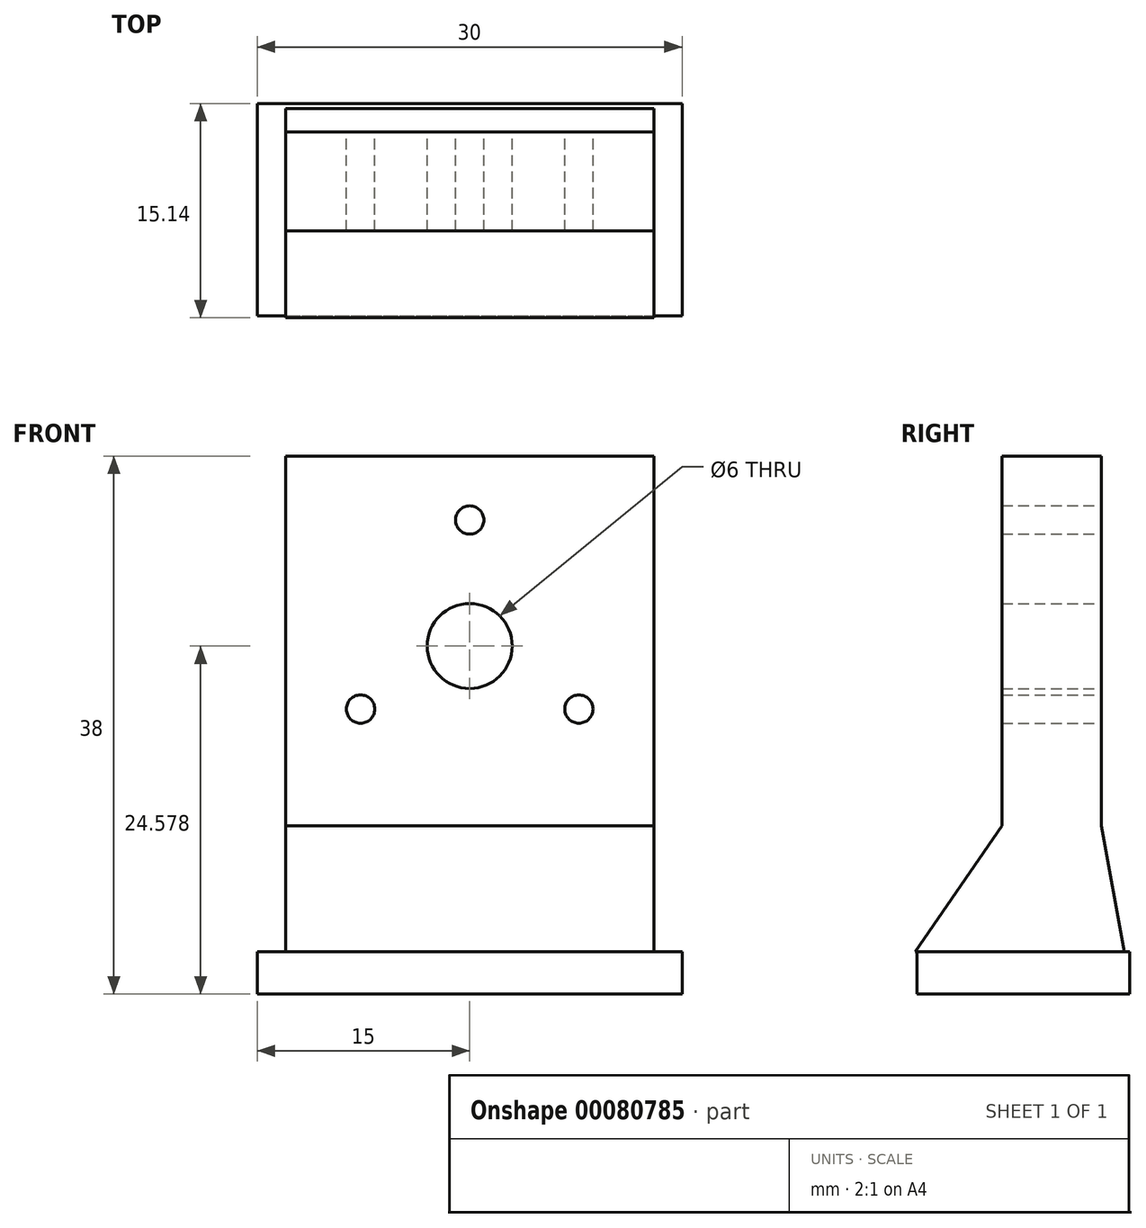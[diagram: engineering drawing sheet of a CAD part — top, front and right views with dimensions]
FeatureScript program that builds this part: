
annotation { "Feature Type Name" : "Feature", "Feature Type Description" : "" }
export const myFeature = defineFeature(function(context is Context, id is Id, definition is map)
    precondition{}
    {
        {
            var Q0;
            Q0=qCreatedBy(makeId("Front.planeOp"),FACE);
            var sketch = newSketch(context, id + "F0", { "sketchPlane" : qUnion([Q0])});
            skLineSegment(sketch, "E0.bottom", {"start": v(-13, 0) * mm, "end": v(13, 0) * mm});
            skLineSegment(sketch, "E0.top", {"start": v(-13, 35) * mm, "end": v(13, 35) * mm});
            skLineSegment(sketch, "E0.left", {"start": v(-13, 0) * mm, "end": v(-13, 35) * mm});
            skLineSegment(sketch, "E0.right", {"start": v(13, 0) * mm, "end": v(13, 35) * mm});
            skPoint(sketch, "E1", {"position": v(0, 0) * mm});
            skCircle(sketch, "E2", {"center": v(0, 21.58) * mm, "radius": 3 * mm});
            skCircle(sketch, "E3", {"center": v(0, 21.58) * mm, "radius": 8.9 * mm, "construction": true});
            skCircle(sketch, "E4", {"center": v(0, 30.48) * mm, "radius": 1 * mm});
            skCircle(sketch, "E5.1.0", {"center": v(-7.7, 17.13) * mm, "radius": 1 * mm});
            skCircle(sketch, "E5.2.0", {"center": v(7.7, 17.13) * mm, "radius": 1 * mm});
            skSolve(sketch);
        }
        {
            var Q0;
            Q0=makeQuery(id+"F0.imprint","IMPRINT",FACE,{"disambiguationData":[TD([[makeQuery(id+"F0.imprint","IMPRINT",EDGE,{"derivedFrom":sQuery(id+"F0.wireOp",EDGE,"E0.bottom")}),1.0]])]});
            extrude(context, id + "F1", {"entities" : qUnion([Q0]), "depth" : 7 * mm});
        }
        {
            var Q0;
            Q0=qCreatedBy(makeId("Top.planeOp"),FACE);
            var sketch = newSketch(context, id + "F2", { "sketchPlane" : qUnion([Q0])});
            skLineSegment(sketch, "E6.bottom", {"start": v(-15, 2) * mm, "end": v(15, 2) * mm});
            skLineSegment(sketch, "E6.top", {"start": v(-15, -13) * mm, "end": v(15, -13) * mm});
            skLineSegment(sketch, "E6.left", {"start": v(-15, 2) * mm, "end": v(-15, -13) * mm});
            skLineSegment(sketch, "E6.right", {"start": v(15, 2) * mm, "end": v(15, -13) * mm});
            skSolve(sketch);
        }
        {
            var Q0;
            Q0=makeQuery(id+"F2.imprint","IMPRINT",FACE,{"disambiguationData":[TD([[makeQuery(id+"F2.imprint","IMPRINT",EDGE,{"derivedFrom":sQuery(id+"F2.wireOp",EDGE,"E6.bottom")}),-1.0]])]});
            extrude(context, id + "F3", {"entities" : qUnion([Q0]), "operationType" : NewBodyOperationType.ADD, "oppositeDirection" : true, "depth" : 3 * mm});
        }
        {
            var Q0;
            Q0=makeQuery(id+"F1.opExtrude","SWEPT_FACE",FACE,{"disambiguationData":[OSD([sQuery(id+"F0.wireOp",EDGE,"E0.left")])]});
            var sketch = newSketch(context, id + "F4", { "sketchPlane" : qUnion([Q0])});
            skLineSegment(sketch, "E7", {"start": v(7, 8.88) * mm, "end": v(13.14, 0) * mm});
            skLineSegment(sketch, "E8", {"start": v(7, 6.87) * mm, "end": v(11.75, 0) * mm});
            skLineSegment(sketch, "E9", {"start": v(7, 4.17) * mm, "end": v(9.88, 0) * mm});
            skLineSegment(sketch, "E10", {"start": v(7, 1.96) * mm, "end": v(8.36, 0) * mm});
            skLineSegment(sketch, "E11", {"start": v(7, 4.17) * mm, "end": v(7, 1.96) * mm});
            skLineSegment(sketch, "E12", {"start": v(7, 8.88) * mm, "end": v(7, 6.87) * mm});
            skLineSegment(sketch, "E13", {"start": v(13.14, 0) * mm, "end": v(11.75, 0) * mm});
            skLineSegment(sketch, "E14", {"start": v(9.88, 0) * mm, "end": v(8.36, 0) * mm});
            skLineSegment(sketch, "E15", {"start": v(0, 8.88) * mm, "end": v(-1.63, 0) * mm});
            skLineSegment(sketch, "E16", {"start": v(0, 4.23) * mm, "end": v(-0.78, 0) * mm});
            skLineSegment(sketch, "E17", {"start": v(0, 8.88) * mm, "end": v(0, 4.23) * mm});
            skLineSegment(sketch, "E18", {"start": v(-1.63, 0) * mm, "end": v(-0.78, 0) * mm});
            skLineSegment(sketch, "E19", {"start": v(-0.78, 0) * mm, "end": v(0, 0) * mm});
            skLineSegment(sketch, "E20", {"start": v(0, 0) * mm, "end": v(0, 4.23) * mm});
            skLineSegment(sketch, "E21", {"start": v(7, 6.87) * mm, "end": v(7, 0) * mm});
            skLineSegment(sketch, "E22", {"start": v(7, 0) * mm, "end": v(11.75, 0) * mm});
            skSolve(sketch);
        }
        {
            var Q0;
            Q0=qSketchRegion(id+"F4",true);
            extrude(context, id + "F5", {"entities" : qUnion([Q0]), "operationType" : NewBodyOperationType.ADD, "oppositeDirection" : true, "depth" : 26 * mm});
        }
    });
